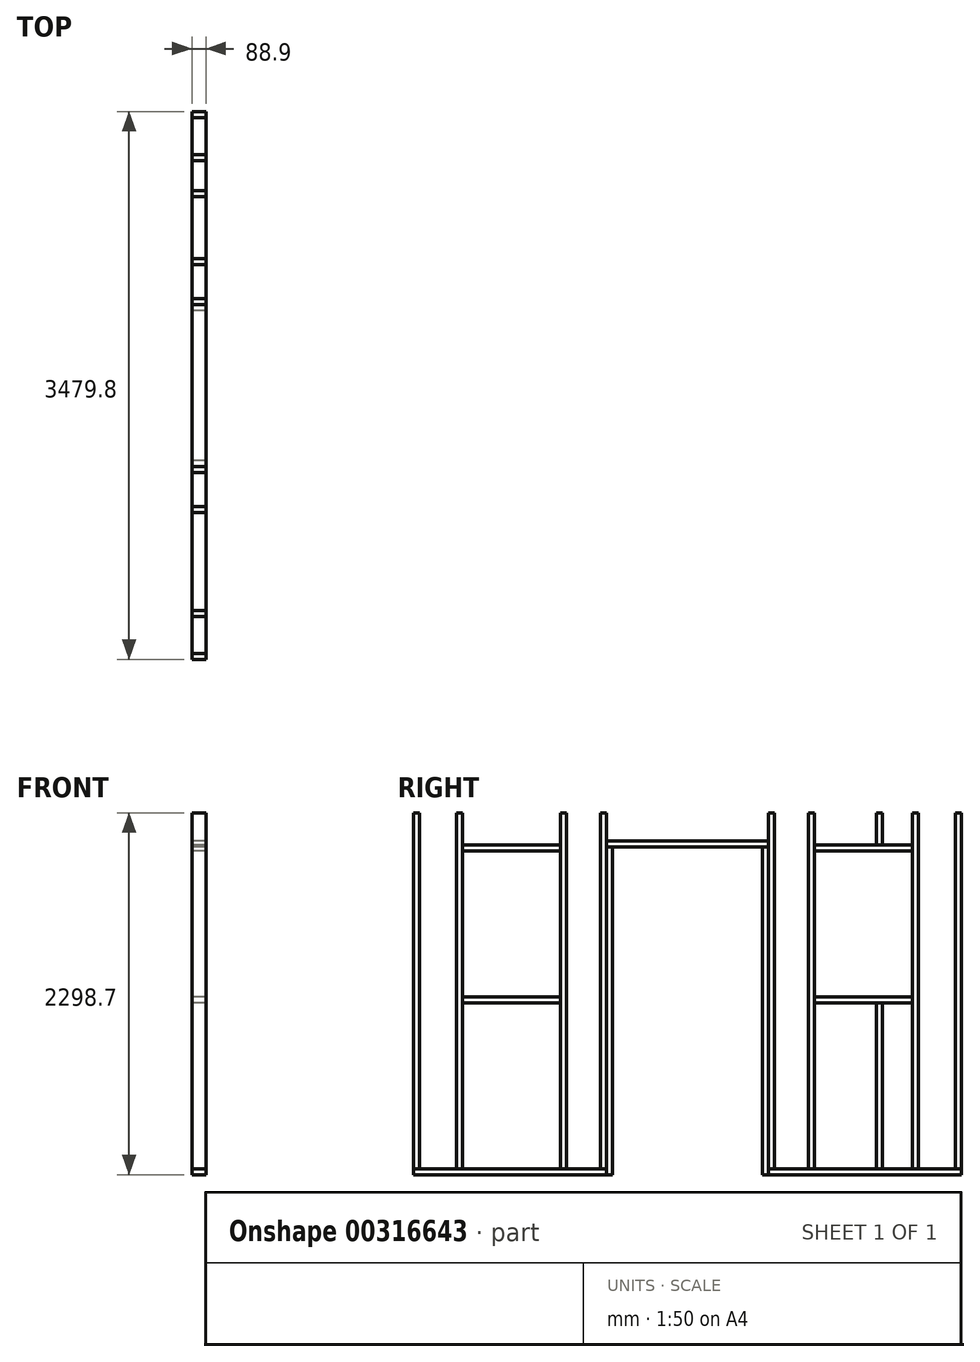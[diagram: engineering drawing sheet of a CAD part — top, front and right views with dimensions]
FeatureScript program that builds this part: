
annotation { "Feature Type Name" : "Feature", "Feature Type Description" : "" }
export const myFeature = defineFeature(function(context is Context, id is Id, definition is map)
    precondition{}
    {
        {
            var Q0;
            Q0=qCreatedBy(makeId("Right.planeOp"),FACE);
            var sketch = newSketch(context, id + "F0", { "sketchPlane" : qUnion([Q0])});
            skLineSegment(sketch, "E0.bottom", {"start": v(-1466.85, 38.1) * mm, "end": v(-1428.75, 38.1) * mm});
            skLineSegment(sketch, "E0.top", {"start": v(-1466.85, 2298.7) * mm, "end": v(-1428.75, 2298.7) * mm});
            skLineSegment(sketch, "E0.left", {"start": v(-1466.85, 38.1) * mm, "end": v(-1466.85, 2298.7) * mm});
            skLineSegment(sketch, "E0.right", {"start": v(-1428.75, 38.1) * mm, "end": v(-1428.75, 2298.7) * mm});
            skLineSegment(sketch, "E1.bottom", {"start": v(-514.35, 38.1) * mm, "end": v(-552.45, 38.1) * mm});
            skLineSegment(sketch, "E1.top", {"start": v(-514.35, 2298.7) * mm, "end": v(-552.45, 2298.7) * mm});
            skLineSegment(sketch, "E1.left", {"start": v(-514.35, 38.1) * mm, "end": v(-514.35, 2298.7) * mm});
            skLineSegment(sketch, "E1.right", {"start": v(-552.45, 38.1) * mm, "end": v(-552.45, 2298.7) * mm});
            skLineSegment(sketch, "E2.bottom", {"start": v(-768.35, 38.1) * mm, "end": v(-806.45, 38.1) * mm});
            skLineSegment(sketch, "E2.top", {"start": v(-768.35, 2298.7) * mm, "end": v(-806.45, 2298.7) * mm});
            skLineSegment(sketch, "E2.left", {"start": v(-768.35, 38.1) * mm, "end": v(-768.35, 2298.7) * mm});
            skLineSegment(sketch, "E2.right", {"start": v(-806.45, 38.1) * mm, "end": v(-806.45, 2298.7) * mm});
            skLineSegment(sketch, "E3.bottom", {"start": v(-1428.75, 2095.5) * mm, "end": v(-806.45, 2095.5) * mm});
            skLineSegment(sketch, "E3.top", {"start": v(-1428.75, 2057.4) * mm, "end": v(-806.45, 2057.4) * mm});
            skLineSegment(sketch, "E3.left", {"start": v(-1428.75, 2095.5) * mm, "end": v(-1428.75, 2057.4) * mm});
            skLineSegment(sketch, "E3.right", {"start": v(-806.45, 2095.5) * mm, "end": v(-806.45, 2057.4) * mm});
            skLineSegment(sketch, "E4.0.1.0", {"start": v(-1428.75, 1130.3) * mm, "end": v(-806.45, 1130.3) * mm});
            skLineSegment(sketch, "E4.0.1.1", {"start": v(-1428.75, 1092.2) * mm, "end": v(-806.45, 1092.2) * mm});
            skLineSegment(sketch, "E4.0.1.2", {"start": v(-1428.75, 1130.3) * mm, "end": v(-1428.75, 1092.2) * mm});
            skLineSegment(sketch, "E4.0.1.3", {"start": v(-806.45, 1130.3) * mm, "end": v(-806.45, 1092.2) * mm});
            skLineSegment(sketch, "E4.direction1", {"start": v(-3426.25, 2057.4) * mm, "end": v(-1428.75, 2057.4) * mm, "construction": true});
            skLineSegment(sketch, "E4.direction2", {"start": v(-1428.75, 2057.4) * mm, "end": v(-1428.75, 1092.2) * mm, "construction": true});
            skLineSegment(sketch, "E5.bottom", {"start": v(-1739.9, 2298.7) * mm, "end": v(-1701.8, 2298.7) * mm});
            skLineSegment(sketch, "E5.top", {"start": v(-1739.9, 38.1) * mm, "end": v(-1701.8, 38.1) * mm});
            skLineSegment(sketch, "E5.left", {"start": v(-1739.9, 2298.7) * mm, "end": v(-1739.9, 38.1) * mm});
            skLineSegment(sketch, "E5.right", {"start": v(-1701.8, 2298.7) * mm, "end": v(-1701.8, 38.1) * mm});
            skLineSegment(sketch, "E6.bottom", {"start": v(-1739.9, 2336.8) * mm, "end": v(1739.9, 2336.8) * mm});
            skLineSegment(sketch, "E6.top", {"start": v(-1739.9, 2298.7) * mm, "end": v(1739.9, 2298.7) * mm});
            skLineSegment(sketch, "E6.left", {"start": v(-1739.9, 2336.8) * mm, "end": v(-1739.9, 2298.7) * mm});
            skLineSegment(sketch, "E6.right", {"start": v(1739.9, 2336.8) * mm, "end": v(1739.9, 2298.7) * mm});
            skPoint(sketch, "E7.endSnap0", {"position": v(0, 2336.8) * mm});
            skPoint(sketch, "E8", {"position": v(-1117.6, 1092.2) * mm});
            skLineSegment(sketch, "E9.bottom", {"start": v(-1739.9, 38.1) * mm, "end": v(-514.35, 38.1) * mm});
            skLineSegment(sketch, "E9.top", {"start": v(-1739.9, 0) * mm, "end": v(-514.35, 0) * mm});
            skLineSegment(sketch, "E9.left", {"start": v(-1739.9, 38.1) * mm, "end": v(-1739.9, 0) * mm});
            skLineSegment(sketch, "E9.right", {"start": v(-514.35, 38.1) * mm, "end": v(-514.35, 0) * mm});
            skLineSegment(sketch, "E10.bottom", {"start": v(-514.35, 2120.9) * mm, "end": v(514.35, 2120.9) * mm});
            skLineSegment(sketch, "E10.top", {"start": v(-514.35, 2082.8) * mm, "end": v(514.35, 2082.8) * mm});
            skLineSegment(sketch, "E10.left", {"start": v(-514.35, 2120.9) * mm, "end": v(-514.35, 2082.8) * mm});
            skLineSegment(sketch, "E10.right", {"start": v(514.35, 2120.9) * mm, "end": v(514.35, 2082.8) * mm});
            skLineSegment(sketch, "E11.bottom", {"start": v(-514.35, 0) * mm, "end": v(-476.25, 0) * mm});
            skLineSegment(sketch, "E11.top", {"start": v(-514.35, 2082.8) * mm, "end": v(-476.25, 2082.8) * mm});
            skLineSegment(sketch, "E11.left", {"start": v(-514.35, 0) * mm, "end": v(-514.35, 2082.8) * mm});
            skLineSegment(sketch, "E11.right", {"start": v(-476.25, 0) * mm, "end": v(-476.25, 2082.8) * mm});
            skLineSegment(sketch, "E12.MirrorCS", {"start": v(1428.75, 2095.5) * mm, "end": v(1428.75, 2057.4) * mm});
            skLineSegment(sketch, "E13.MirrorCS", {"start": v(806.45, 2095.5) * mm, "end": v(806.45, 2057.4) * mm});
            skLineSegment(sketch, "E14.MirrorCS", {"start": v(1428.75, 2095.5) * mm, "end": v(806.45, 2095.5) * mm});
            skLineSegment(sketch, "E15.MirrorCS", {"start": v(1428.75, 2057.4) * mm, "end": v(806.45, 2057.4) * mm});
            skLineSegment(sketch, "E16.MirrorCS", {"start": v(1428.75, 2057.4) * mm, "end": v(1428.75, 1092.2) * mm, "construction": true});
            skLineSegment(sketch, "E17.MirrorCS", {"start": v(3426.25, 2057.4) * mm, "end": v(1428.75, 2057.4) * mm, "construction": true});
            skLineSegment(sketch, "E18.MirrorCS", {"start": v(1739.9, 38.1) * mm, "end": v(1739.9, 0) * mm});
            skLineSegment(sketch, "E19.MirrorCS", {"start": v(514.35, 38.1) * mm, "end": v(552.45, 38.1) * mm});
            skLineSegment(sketch, "E20.MirrorCS", {"start": v(514.35, 38.1) * mm, "end": v(514.35, 0) * mm});
            skLineSegment(sketch, "E21.MirrorCS", {"start": v(1739.9, 38.1) * mm, "end": v(1701.8, 38.1) * mm});
            skLineSegment(sketch, "E22.MirrorCS", {"start": v(514.35, 0) * mm, "end": v(476.25, 0) * mm});
            skLineSegment(sketch, "E23.MirrorCS", {"start": v(1428.75, 1130.3) * mm, "end": v(1428.75, 1092.2) * mm});
            skLineSegment(sketch, "E24.MirrorCS", {"start": v(1466.85, 38.1) * mm, "end": v(1428.75, 38.1) * mm});
            skLineSegment(sketch, "E25.MirrorCS", {"start": v(768.35, 38.1) * mm, "end": v(806.45, 38.1) * mm});
            skLineSegment(sketch, "E26.MirrorCS", {"start": v(806.45, 1130.3) * mm, "end": v(806.45, 1092.2) * mm});
            skLineSegment(sketch, "E27.MirrorCS", {"start": v(514.35, 38.1) * mm, "end": v(514.35, 2298.7) * mm});
            skLineSegment(sketch, "E28.MirrorCS", {"start": v(1428.75, 1130.3) * mm, "end": v(806.45, 1130.3) * mm});
            skLineSegment(sketch, "E29.MirrorCS", {"start": v(476.25, 0) * mm, "end": v(476.25, 2082.8) * mm});
            skLineSegment(sketch, "E30.MirrorCS", {"start": v(552.45, 38.1) * mm, "end": v(552.45, 2298.7) * mm});
            skLineSegment(sketch, "E31.MirrorCS", {"start": v(806.45, 38.1) * mm, "end": v(806.45, 2298.7) * mm});
            skLineSegment(sketch, "E32.MirrorCS", {"start": v(1428.75, 38.1) * mm, "end": v(1428.75, 2298.7) * mm});
            skLineSegment(sketch, "E33.MirrorCS", {"start": v(1739.9, 2298.7) * mm, "end": v(1739.9, 38.1) * mm});
            skLineSegment(sketch, "E34.MirrorCS", {"start": v(514.35, 0) * mm, "end": v(514.35, 2082.8) * mm});
            skLineSegment(sketch, "E35.MirrorCS", {"start": v(1428.75, 1092.2) * mm, "end": v(806.45, 1092.2) * mm});
            skLineSegment(sketch, "E36.MirrorCS", {"start": v(1701.8, 2298.7) * mm, "end": v(1701.8, 38.1) * mm});
            skLineSegment(sketch, "E37.MirrorCS", {"start": v(1739.9, 0) * mm, "end": v(514.35, 0) * mm});
            skPoint(sketch, "E38.MirrorP", {"position": v(1117.6, 1092.2) * mm});
            skLineSegment(sketch, "E39.MirrorCS", {"start": v(768.35, 38.1) * mm, "end": v(768.35, 2298.7) * mm});
            skLineSegment(sketch, "E40.MirrorCS", {"start": v(1739.9, 38.1) * mm, "end": v(514.35, 38.1) * mm});
            skLineSegment(sketch, "E41.MirrorCS", {"start": v(1466.85, 38.1) * mm, "end": v(1466.85, 2298.7) * mm});
            skLineSegment(sketch, "E42.bottom", {"start": v(-1238.25, 2298.7) * mm, "end": v(-1200.15, 2298.7) * mm});
            skLineSegment(sketch, "E42.top", {"start": v(-1238.25, 2095.5) * mm, "end": v(-1200.15, 2095.5) * mm});
            skLineSegment(sketch, "E42.left", {"start": v(-1238.25, 2298.7) * mm, "end": v(-1238.25, 2095.5) * mm});
            skLineSegment(sketch, "E42.right", {"start": v(-1200.15, 2298.7) * mm, "end": v(-1200.15, 2095.5) * mm});
            skLineSegment(sketch, "E43.bottom", {"start": v(-1238.25, 1092.2) * mm, "end": v(-1200.15, 1092.2) * mm});
            skLineSegment(sketch, "E43.top", {"start": v(-1238.25, 38.1) * mm, "end": v(-1200.15, 38.1) * mm});
            skLineSegment(sketch, "E43.left", {"start": v(-1238.25, 1092.2) * mm, "end": v(-1238.25, 38.1) * mm});
            skLineSegment(sketch, "E43.right", {"start": v(-1200.15, 1092.2) * mm, "end": v(-1200.15, 38.1) * mm});
            skPoint(sketch, "E44", {"position": v(-1219.2, 2298.7) * mm});
            skLineSegment(sketch, "E45.bottom", {"start": v(-19.05, 2298.7) * mm, "end": v(19.05, 2298.7) * mm});
            skLineSegment(sketch, "E45.top", {"start": v(-19.05, 2120.9) * mm, "end": v(19.05, 2120.9) * mm});
            skLineSegment(sketch, "E45.left", {"start": v(-19.05, 2298.7) * mm, "end": v(-19.05, 2120.9) * mm});
            skLineSegment(sketch, "E45.right", {"start": v(19.05, 2298.7) * mm, "end": v(19.05, 2120.9) * mm});
            skPoint(sketch, "E46", {"position": v(0, 2298.7) * mm});
            skLineSegment(sketch, "E47.MirrorCS", {"start": v(1200.15, 1092.2) * mm, "end": v(1200.15, 38.1) * mm});
            skLineSegment(sketch, "E48.MirrorCS", {"start": v(1238.25, 1092.2) * mm, "end": v(1238.25, 38.1) * mm});
            skLineSegment(sketch, "E49.MirrorCS", {"start": v(1238.25, 2298.7) * mm, "end": v(1238.25, 2095.5) * mm});
            skLineSegment(sketch, "E50.MirrorCS", {"start": v(1200.15, 2298.7) * mm, "end": v(1200.15, 2095.5) * mm});
            skSolve(sketch);
        }
        {
            var Q0;
            {var subQ0=sQuery(id+"F0.wireOp",EDGE,"E5.left");Q0=makeQuery(id+"F0.imprint","IMPRINT",FACE,{"disambiguationData":[TD([[makeQuery(id+"F0.imprint","IMPRINT",EDGE,{"derivedFrom":subQ0}),1.0]])]});}
            var Q1;
            {var subQ7=sQuery(id+"F0.wireOp",EDGE,"E0.left");Q1=makeQuery(id+"F0.imprint","IMPRINT",FACE,{"disambiguationData":[TD([[makeQuery(id+"F0.imprint","IMPRINT",EDGE,{"derivedFrom":subQ7}),-1.0]])]});}
            var Q2;
            {var subQ5=sQuery(id+"F0.wireOp",EDGE,"E2.left");Q2=makeQuery(id+"F0.imprint","IMPRINT",FACE,{"disambiguationData":[TD([[makeQuery(id+"F0.imprint","IMPRINT",EDGE,{"derivedFrom":subQ5}),1.0]])]});}
            var Q3;
            {var subQ1=sQuery(id+"F0.wireOp",EDGE,"E1.left");Q3=makeQuery(id+"F0.imprint","IMPRINT",FACE,{"disambiguationData":[TD([[makeQuery(id+"F0.imprint","IMPRINT",EDGE,{"derivedFrom":subQ1}),1.0]])]});}
            var Q4;
            {var subQ6=sQuery(id+"F0.wireOp",EDGE,"E30.MirrorCS");Q4=makeQuery(id+"F0.imprint","IMPRINT",FACE,{"disambiguationData":[TD([[makeQuery(id+"F0.imprint","IMPRINT",EDGE,{"derivedFrom":subQ6}),1.0]])]});}
            var Q5;
            {var subQ8=sQuery(id+"F0.wireOp",EDGE,"E39.MirrorCS");Q5=makeQuery(id+"F0.imprint","IMPRINT",FACE,{"disambiguationData":[TD([[makeQuery(id+"F0.imprint","IMPRINT",EDGE,{"derivedFrom":subQ8}),-1.0]])]});}
            var Q6;
            {var subQ8=sQuery(id+"F0.wireOp",EDGE,"E41.MirrorCS");Q6=makeQuery(id+"F0.imprint","IMPRINT",FACE,{"disambiguationData":[TD([[makeQuery(id+"F0.imprint","IMPRINT",EDGE,{"derivedFrom":subQ8}),1.0]])]});}
            var Q7;
            {var subQ0=sQuery(id+"F0.wireOp",EDGE,"E33.MirrorCS");Q7=makeQuery(id+"F0.imprint","IMPRINT",FACE,{"disambiguationData":[TD([[makeQuery(id+"F0.imprint","IMPRINT",EDGE,{"derivedFrom":subQ0}),-1.0]])]});}
            var Q8;
            Q8=makeQuery(id+"F0.imprint","IMPRINT",FACE,{"disambiguationData":[TD([[makeQuery(id+"F0.imprint","IMPRINT",EDGE,{"derivedFrom":sQuery(id+"F0.wireOp",EDGE,"E43.bottom")}),-1.0]])]});
            var Q9;
            Q9=makeQuery(id+"F0.imprint","IMPRINT",FACE,{"disambiguationData":[TD([[makeQuery(id+"F0.imprint","IMPRINT",EDGE,{"derivedFrom":sQuery(id+"F0.wireOp",EDGE,"E42.bottom")}),-1.0]])]});
            var Q10;
            Q10=makeQuery(id+"F0.imprint","IMPRINT",FACE,{"disambiguationData":[TD([[makeQuery(id+"F0.imprint","IMPRINT",EDGE,{"derivedFrom":sQuery(id+"F0.wireOp",EDGE,"E45.bottom")}),-1.0]])]});
            var Q11;
            {var subQ0=sQuery(id+"F0.wireOp",EDGE,"E49.MirrorCS");Q11=makeQuery(id+"F0.imprint","IMPRINT",FACE,{"disambiguationData":[TD([[makeQuery(id+"F0.imprint","IMPRINT",EDGE,{"derivedFrom":subQ0}),-1.0]])]});}
            var Q12;
            {var subQ0=sQuery(id+"F0.wireOp",EDGE,"E47.MirrorCS");Q12=makeQuery(id+"F0.imprint","IMPRINT",FACE,{"disambiguationData":[TD([[makeQuery(id+"F0.imprint","IMPRINT",EDGE,{"derivedFrom":subQ0}),1.0]])]});}
            extrude(context, id + "F1", {"entities" : qUnion([Q0, Q1, Q2, Q3, Q4, Q5, Q6, Q7, Q8, Q9, Q10, Q11, Q12]), "depth" : 88.9 * mm});
        }
        {
            var Q0;
            Q0=makeQuery(id+"F0.imprint","IMPRINT",FACE,{"disambiguationData":[TD([[makeQuery(id+"F0.imprint","IMPRINT",EDGE,{"derivedFrom":sQuery(id+"F0.wireOp",EDGE,"E3.bottom")}),-1.0]])]});
            var Q1;
            Q1=makeQuery(id+"F0.imprint","IMPRINT",FACE,{"disambiguationData":[TD([[makeQuery(id+"F0.imprint","IMPRINT",EDGE,{"derivedFrom":sQuery(id+"F0.wireOp",EDGE,"E6.bottom")}),-1.0]])]});
            var Q2;
            {var subQ4=sQuery(id+"F0.wireOp",EDGE,"E10.bottom");Q2=makeQuery(id+"F0.imprint","IMPRINT",FACE,{"disambiguationData":[TD([[makeQuery(id+"F0.imprint","IMPRINT",EDGE,{"derivedFrom":subQ4}),-1.0]])]});}
            var Q3;
            {var subQ0=sQuery(id+"F0.wireOp",EDGE,"E14.MirrorCS");Q3=makeQuery(id+"F0.imprint","IMPRINT",FACE,{"disambiguationData":[TD([[makeQuery(id+"F0.imprint","IMPRINT",EDGE,{"derivedFrom":subQ0}),1.0]])]});}
            var Q4;
            Q4=makeQuery(id+"F0.imprint","IMPRINT",FACE,{"disambiguationData":[TD([[makeQuery(id+"F0.imprint","IMPRINT",EDGE,{"derivedFrom":sQuery(id+"F0.wireOp",EDGE,"E4.0.1.0")}),-1.0]])]});
            var Q5;
            {var subQ9=sQuery(id+"F0.wireOp",EDGE,"E9.top");Q5=makeQuery(id+"F0.imprint","IMPRINT",FACE,{"disambiguationData":[TD([[makeQuery(id+"F0.imprint","IMPRINT",EDGE,{"derivedFrom":subQ9}),1.0]])]});}
            var Q6;
            {var subQ1=sQuery(id+"F0.wireOp",EDGE,"E18.MirrorCS");Q6=makeQuery(id+"F0.imprint","IMPRINT",FACE,{"disambiguationData":[TD([[makeQuery(id+"F0.imprint","IMPRINT",EDGE,{"derivedFrom":subQ1}),-1.0]])]});}
            var Q7;
            {var subQ0=sQuery(id+"F0.wireOp",EDGE,"E28.MirrorCS");Q7=makeQuery(id+"F0.imprint","IMPRINT",FACE,{"disambiguationData":[TD([[makeQuery(id+"F0.imprint","IMPRINT",EDGE,{"derivedFrom":subQ0}),1.0]])]});}
            extrude(context, id + "F2", {"entities" : qUnion([Q0, Q1, Q2, Q3, Q4, Q5, Q6, Q7]), "depth" : 88.9 * mm});
        }
        {
            var Q0;
            {var subQ3=sQuery(id+"F0.wireOp",EDGE,"E11.bottom");Q0=makeQuery(id+"F0.imprint","IMPRINT",FACE,{"disambiguationData":[TD([[makeQuery(id+"F0.imprint","IMPRINT",EDGE,{"derivedFrom":subQ3}),1.0]])]});}
            var Q1;
            {var subQ1=sQuery(id+"F0.wireOp",EDGE,"E22.MirrorCS");Q1=makeQuery(id+"F0.imprint","IMPRINT",FACE,{"disambiguationData":[TD([[makeQuery(id+"F0.imprint","IMPRINT",EDGE,{"derivedFrom":subQ1}),-1.0]])]});}
            extrude(context, id + "F3", {"entities" : qUnion([Q0, Q1]), "depth" : 88.9 * mm});
        }
    });
